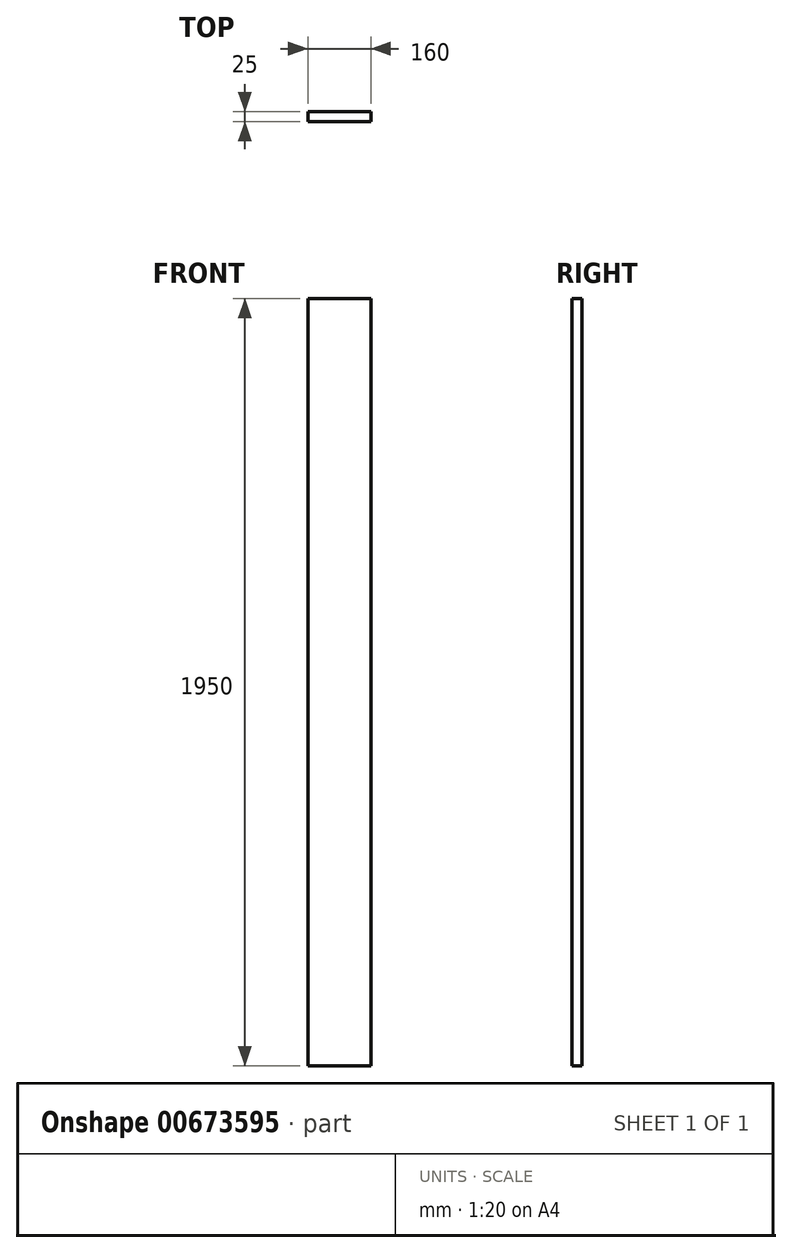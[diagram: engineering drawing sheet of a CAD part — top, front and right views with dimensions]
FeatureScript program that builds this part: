
annotation { "Feature Type Name" : "Feature", "Feature Type Description" : "" }
export const myFeature = defineFeature(function(context is Context, id is Id, definition is map)
    precondition{}
    {
        {
            var Q0;
            Q0=qCreatedBy(makeId("Top.planeOp"),FACE);
            var sketch = newSketch(context, id + "F0", { "sketchPlane" : qUnion([Q0])});
            skLineSegment(sketch, "E0.bottom", {"start": v(80, -12.5) * mm, "end": v(-80, -12.5) * mm});
            skLineSegment(sketch, "E0.top", {"start": v(80, 12.5) * mm, "end": v(-80, 12.5) * mm});
            skLineSegment(sketch, "E0.left", {"start": v(80, -12.5) * mm, "end": v(80, 12.5) * mm});
            skLineSegment(sketch, "E0.right", {"start": v(-80, -12.5) * mm, "end": v(-80, 12.5) * mm});
            skPoint(sketch, "E0.middle", {"position": v(0, 0) * mm});
            skSolve(sketch);
        }
        {
            var Q0;
            Q0=makeQuery(id+"F0.imprint","IMPRINT",FACE,{"disambiguationData":[TD([[makeQuery(id+"F0.imprint","IMPRINT",EDGE,{"derivedFrom":sQuery(id+"F0.wireOp",EDGE,"E0.bottom")}),-1.0]])]});
            extrude(context, id + "F1", {"entities" : qUnion([Q0]), "depth" : 1950 * mm, "offsetDistance" : 25 * mm});
        }
    });
